# Revit family: Dental_Equipment-Midmark-Sterilizer_M9-050
name_source: partatom
category: Specialty Equipment
units: mm (PartAtom-declared; Revit-internal decimal feet)

## family parameters
Always vertical = Yes
Cut with Voids When Loaded = No
OmniClass Number = 23.40.70.11.14.11
OmniClass Title = Medical Equipment
Part Type = Normal
Room Calculation Point = No
Round Connector Dimension = Use Diameter
Shared = No
Work Plane-Based = No

## types (1)
- M9-050
    Apparent Load = 1380 VA
    Chamber = 22.9 cm dia. x 38.1 cm deep (9 in dia. x 15 in deep)
    Connector Description = 115 V/50 – 60 Hz/12 A
    Current = 12 A
    Default Elevation = 0 cm
    Description = Midmark® Steam Sterilizers
    Heat Emission = 5275 kJ (5000 BTU)/ hr during operation
    Height = 42.2 cm
    Length = 52 cm
    Manufacturer = Midmark
    Min Support Surface = 50.3 cm x 59.7 cm (19.8 in x 23.5 in)
    Model = M9
    Number of Poles = 1
    Power Factor = 1
    Product Page URL = https://www.midmark.com
    Product data url = https://bimobject.com
    URL = https://www.midmark.com
    Version = 1
    Voltage = 115 V
    Water Reservoir Capacity = 4.1 liters (1.1 gallons) to Full Mark
    Weight = 82.00 lbf
    Width = 40.1 cm

## geometry (parser evidence)
native form markers: Sweep x3
no freeform markers — native parametric forms only
